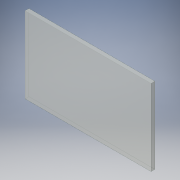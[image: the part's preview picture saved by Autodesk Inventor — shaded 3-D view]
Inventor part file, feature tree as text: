
AUTODESK INVENTOR PART (.ipt)
format: ipt  version: 2016 (Build 200138000, 138)  size: 93,184 bytes
history: native  units: in
note: dims shown in document units (in); Inventor stores cm internally (conversion verified against a paired STEP export)
features: extrude x1, sketch x1
ambient origin geometry x8: Origin, YZ Plane, XZ Plane, XY Plane, X Axis, Y Axis, Z Axis, Center Point
bodies: Solid1 (feature_tree)
feature tree (2):
  extrude  "Extrusion1"  [1 undecoded]
  sketch  "Sketch1"  dims[d3=0.0in]
note: 1 required parameter value undecoded (feature->parameter linkage not recoverable at this tier; creation-order binding heuristic only, values carry confidence <= 0.55)
